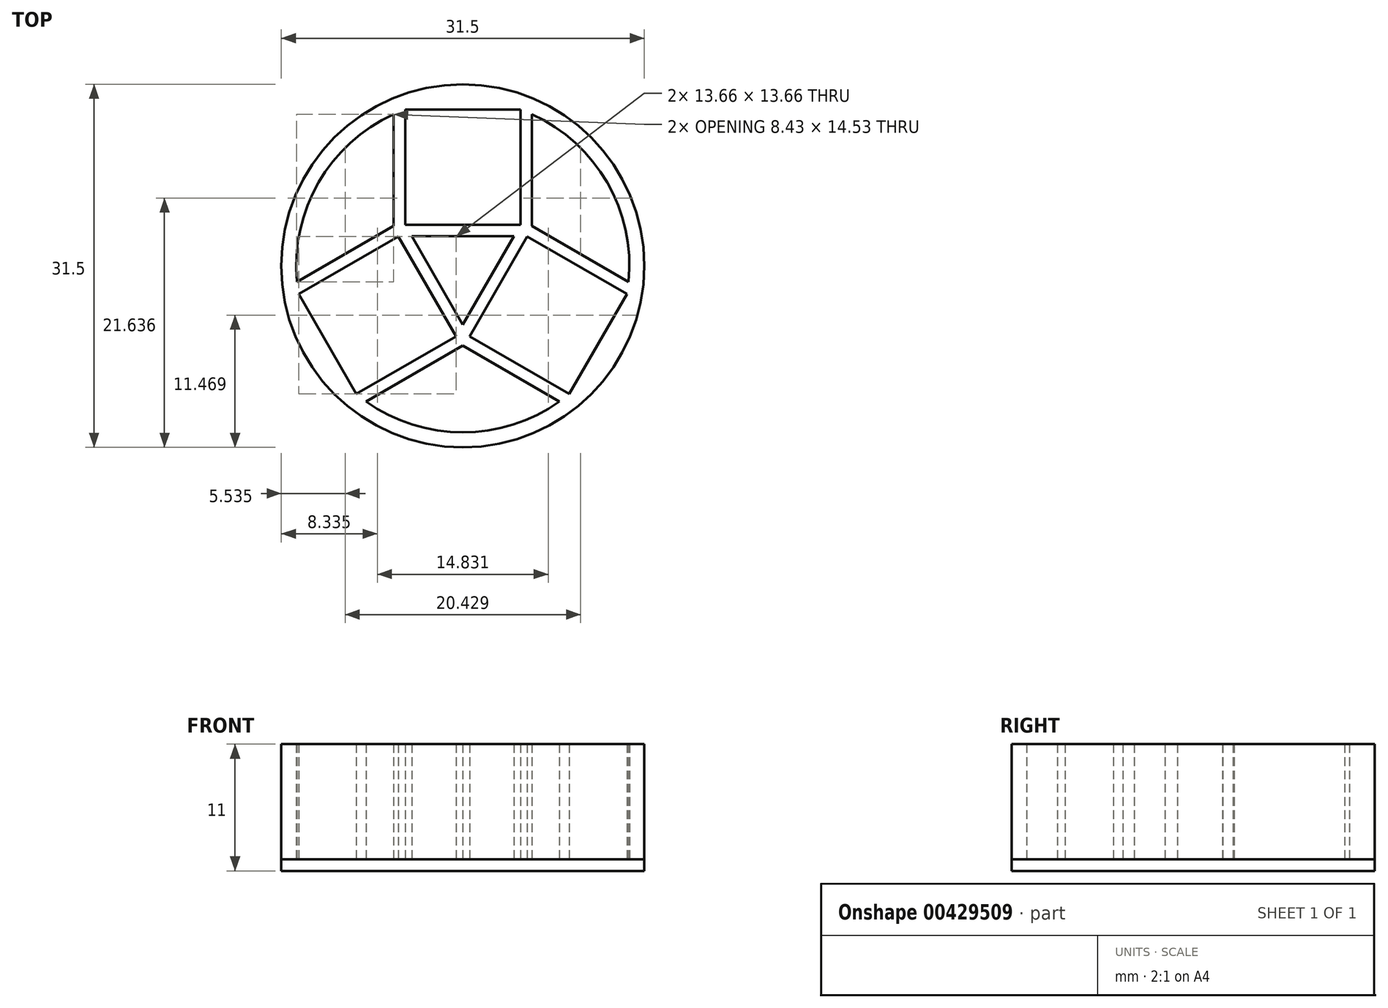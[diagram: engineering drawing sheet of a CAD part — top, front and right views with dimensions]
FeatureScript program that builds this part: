
annotation { "Feature Type Name" : "Feature", "Feature Type Description" : "" }
export const myFeature = defineFeature(function(context is Context, id is Id, definition is map)
    precondition{}
    {
        {
            var Q0;
            Q0=qCreatedBy(makeId("Top.planeOp"),FACE);
            var sketch = newSketch(context, id + "F0", { "sketchPlane" : qUnion([Q0])});
            skLineSegment(sketch, "E0.bottom", {"start": v(-5, 13.56) * mm, "end": v(5, 13.56) * mm});
            skLineSegment(sketch, "E0.top", {"start": v(-5, 3.56) * mm, "end": v(5, 3.56) * mm});
            skLineSegment(sketch, "E0.left", {"start": v(-5, 13.56) * mm, "end": v(-5, 3.56) * mm});
            skLineSegment(sketch, "E0.right", {"start": v(5, 13.56) * mm, "end": v(5, 3.56) * mm});
            skCircle(sketch, "E1", {"center": v(0, 0) * mm, "radius": 15.75 * mm});
            skLineSegment(sketch, "E2.0", {"start": v(-6, 14.56) * mm, "end": v(6, 14.56) * mm});
            skLineSegment(sketch, "E2.1", {"start": v(-6, 14.56) * mm, "end": v(-6, 2.56) * mm});
            skLineSegment(sketch, "E2.2", {"start": v(-6, 2.56) * mm, "end": v(6, 2.56) * mm});
            skLineSegment(sketch, "E2.3", {"start": v(6, 14.56) * mm, "end": v(6, 2.56) * mm});
            skLineSegment(sketch, "E3.1.0", {"start": v(-9.61, -12.48) * mm, "end": v(0.78, -6.48) * mm});
            skLineSegment(sketch, "E3.1.1", {"start": v(-9.25, -11.11) * mm, "end": v(-0.59, -6.11) * mm});
            skLineSegment(sketch, "E3.1.2", {"start": v(-9.61, -12.48) * mm, "end": v(-15.61, -2.09) * mm});
            skLineSegment(sketch, "E3.1.3", {"start": v(-9.25, -11.11) * mm, "end": v(-14.25, -2.45) * mm});
            skLineSegment(sketch, "E3.1.4", {"start": v(-14.25, -2.45) * mm, "end": v(-5.59, 2.55) * mm});
            skLineSegment(sketch, "E3.1.5", {"start": v(-15.61, -2.09) * mm, "end": v(-5.22, 3.91) * mm});
            skLineSegment(sketch, "E3.1.6", {"start": v(0.78, -6.48) * mm, "end": v(-5.22, 3.91) * mm});
            skLineSegment(sketch, "E3.1.7", {"start": v(-0.59, -6.11) * mm, "end": v(-5.59, 2.55) * mm});
            skLineSegment(sketch, "E3.2.0", {"start": v(15.61, -2.09) * mm, "end": v(5.22, 3.91) * mm});
            skLineSegment(sketch, "E3.2.1", {"start": v(14.25, -2.45) * mm, "end": v(5.59, 2.55) * mm});
            skLineSegment(sketch, "E3.2.2", {"start": v(15.61, -2.09) * mm, "end": v(9.61, -12.48) * mm});
            skLineSegment(sketch, "E3.2.3", {"start": v(14.25, -2.45) * mm, "end": v(9.25, -11.11) * mm});
            skLineSegment(sketch, "E3.2.4", {"start": v(9.25, -11.11) * mm, "end": v(0.59, -6.11) * mm});
            skLineSegment(sketch, "E3.2.5", {"start": v(9.61, -12.48) * mm, "end": v(-0.78, -6.48) * mm});
            skLineSegment(sketch, "E3.2.6", {"start": v(5.22, 3.91) * mm, "end": v(-0.78, -6.48) * mm});
            skLineSegment(sketch, "E3.2.7", {"start": v(5.59, 2.55) * mm, "end": v(0.59, -6.11) * mm});
            skCircle(sketch, "E4", {"center": v(0, 0) * mm, "radius": 14.45 * mm});
            skSolve(sketch);
        }
        {
            var Q0;
            {var subQ5=sQuery(id+"F0.wireOp",EDGE,"E3.1.2");Q0=makeQuery(id+"F0.imprint","IMPRINT",FACE,{"disambiguationData":[TD([[makeQuery(id+"F0.imprint","IMPRINT",EDGE,{"derivedFrom":subQ5}),-1.0]])]});}
            var Q1;
            {var subQ5=sQuery(id+"F0.wireOp",EDGE,"E3.2.2");Q1=makeQuery(id+"F0.imprint","IMPRINT",FACE,{"disambiguationData":[TD([[makeQuery(id+"F0.imprint","IMPRINT",EDGE,{"derivedFrom":subQ5}),-1.0]])]});}
            var Q2;
            Q2=makeQuery(id+"F0.imprint","IMPRINT",FACE,{"disambiguationData":[TD([[makeQuery(id+"F0.imprint","IMPRINT",EDGE,{"derivedFrom":sQuery(id+"F0.wireOp",EDGE,"E0.top")}),-1.0]])]});
            var Q3;
            {var subQ0=sQuery(id+"F0.wireOp",EDGE,"E4");var subQ1=sQuery(id+"F0.wireOp",EDGE,"E2.1");var subQ2=makeQuery(id+"F0.imprint","INTERSECT",VERTEX,{"derivedFrom":[subQ1,subQ0]});Q3=makeQuery(id+"F0.imprint","IMPRINT",FACE,{"disambiguationData":[TD([[makeQuery(id+"F0.imprint","IMPRINT",EDGE,{"disambiguationData":[TD([[subQ2,-1.0]])],"derivedFrom":subQ1}),-1.0]])]});}
            var Q4;
            {var subQ0=sQuery(id+"F0.wireOp",EDGE,"E3.1.0");var subQ5=sQuery(id+"F0.wireOp",EDGE,"E4");var subQ6=makeQuery(id+"F0.imprint","INTERSECT",VERTEX,{"derivedFrom":[subQ0,subQ5]});Q4=makeQuery(id+"F0.imprint","IMPRINT",FACE,{"disambiguationData":[TD([[makeQuery(id+"F0.imprint","IMPRINT",EDGE,{"disambiguationData":[TD([[subQ6,-1.0]])],"derivedFrom":subQ5}),-1.0]])]});}
            var Q5;
            {var subQ0=sQuery(id+"F0.wireOp",EDGE,"E2.3");var subQ5=sQuery(id+"F0.wireOp",EDGE,"E4");var subQ7=makeQuery(id+"F0.imprint","INTERSECT",VERTEX,{"derivedFrom":[subQ0,subQ5]});Q5=makeQuery(id+"F0.imprint","IMPRINT",FACE,{"disambiguationData":[TD([[makeQuery(id+"F0.imprint","IMPRINT",EDGE,{"disambiguationData":[TD([[subQ7,1.0]])],"derivedFrom":subQ5}),-1.0]])]});}
            var Q6;
            {var subQ0=sQuery(id+"F0.wireOp",EDGE,"E3.1.6");var subQ1=sQuery(id+"F0.wireOp",EDGE,"E2.2");var subQ2=makeQuery(id+"F0.imprint","INTERSECT",VERTEX,{"derivedFrom":[subQ1,subQ0]});Q6=makeQuery(id+"F0.imprint","IMPRINT",FACE,{"disambiguationData":[TD([[makeQuery(id+"F0.imprint","IMPRINT",EDGE,{"disambiguationData":[TD([[subQ2,-1.0]])],"derivedFrom":subQ1}),-1.0]])]});}
            var Q7;
            {var subQ0=sQuery(id+"F0.wireOp",EDGE,"E2.0");Q7=makeQuery(id+"F0.imprint","IMPRINT",FACE,{"disambiguationData":[TD([[makeQuery(id+"F0.imprint","IMPRINT",EDGE,{"derivedFrom":subQ0}),1.0]])]});}
            var Q8;
            {var subQ0=sQuery(id+"F0.wireOp",EDGE,"E3.1.2");Q8=makeQuery(id+"F0.imprint","IMPRINT",FACE,{"disambiguationData":[TD([[makeQuery(id+"F0.imprint","IMPRINT",EDGE,{"derivedFrom":subQ0}),1.0]])]});}
            var Q9;
            {var subQ0=sQuery(id+"F0.wireOp",EDGE,"E3.2.2");Q9=makeQuery(id+"F0.imprint","IMPRINT",FACE,{"disambiguationData":[TD([[makeQuery(id+"F0.imprint","IMPRINT",EDGE,{"derivedFrom":subQ0}),1.0]])]});}
            var Q10;
            Q10=makeQuery(id+"F0.imprint","IMPRINT",FACE,{"disambiguationData":[TD([[makeQuery(id+"F0.imprint","IMPRINT",EDGE,{"derivedFrom":sQuery(id+"F0.wireOp",EDGE,"E0.bottom")}),-1.0]])]});
            var Q11;
            {var subQ0=sQuery(id+"F0.wireOp",EDGE,"E0.bottom");Q11=makeQuery(id+"F0.imprint","IMPRINT",FACE,{"disambiguationData":[TD([[makeQuery(id+"F0.imprint","IMPRINT",EDGE,{"derivedFrom":subQ0}),1.0]])]});}
            var Q12;
            Q12=makeQuery(id+"F0.imprint","IMPRINT",FACE,{"disambiguationData":[TD([[makeQuery(id+"F0.imprint","IMPRINT",EDGE,{"derivedFrom":sQuery(id+"F0.wireOp",EDGE,"E3.1.1")}),1.0]])]});
            var Q13;
            {var subQ0=sQuery(id+"F0.wireOp",EDGE,"E3.1.3");Q13=makeQuery(id+"F0.imprint","IMPRINT",FACE,{"disambiguationData":[TD([[makeQuery(id+"F0.imprint","IMPRINT",EDGE,{"derivedFrom":subQ0}),1.0]])]});}
            var Q14;
            Q14=makeQuery(id+"F0.imprint","IMPRINT",FACE,{"disambiguationData":[TD([[makeQuery(id+"F0.imprint","IMPRINT",EDGE,{"derivedFrom":sQuery(id+"F0.wireOp",EDGE,"E3.2.1")}),1.0]])]});
            var Q15;
            {var subQ0=sQuery(id+"F0.wireOp",EDGE,"E3.2.3");Q15=makeQuery(id+"F0.imprint","IMPRINT",FACE,{"disambiguationData":[TD([[makeQuery(id+"F0.imprint","IMPRINT",EDGE,{"derivedFrom":subQ0}),1.0]])]});}
            var Q16;
            {var subQ0=sQuery(id+"F0.wireOp",EDGE,"E2.1");var subQ5=sQuery(id+"F0.wireOp",EDGE,"E4");var subQ6=makeQuery(id+"F0.imprint","INTERSECT",VERTEX,{"derivedFrom":[subQ0,subQ5]});Q16=makeQuery(id+"F0.imprint","IMPRINT",FACE,{"disambiguationData":[TD([[makeQuery(id+"F0.imprint","IMPRINT",EDGE,{"disambiguationData":[TD([[subQ6,-1.0]])],"derivedFrom":subQ5}),-1.0]])]});}
            var Q17;
            {var subQ7=sQuery(id+"F0.wireOp",EDGE,"E3.1.1");Q17=makeQuery(id+"F0.imprint","IMPRINT",FACE,{"disambiguationData":[TD([[makeQuery(id+"F0.imprint","IMPRINT",EDGE,{"derivedFrom":subQ7}),-1.0]])]});}
            var Q18;
            {var subQ0=sQuery(id+"F0.wireOp",EDGE,"E4");var subQ1=sQuery(id+"F0.wireOp",EDGE,"E2.3");var subQ2=makeQuery(id+"F0.imprint","INTERSECT",VERTEX,{"derivedFrom":[subQ1,subQ0]});Q18=makeQuery(id+"F0.imprint","IMPRINT",FACE,{"disambiguationData":[TD([[makeQuery(id+"F0.imprint","IMPRINT",EDGE,{"disambiguationData":[TD([[subQ2,-1.0]])],"derivedFrom":subQ1}),1.0]])]});}
            var Q19;
            {var subQ16=sQuery(id+"F0.wireOp",EDGE,"E3.2.1");Q19=makeQuery(id+"F0.imprint","IMPRINT",FACE,{"disambiguationData":[TD([[makeQuery(id+"F0.imprint","IMPRINT",EDGE,{"derivedFrom":subQ16}),-1.0]])]});}
            var Q20;
            {var subQ0=sQuery(id+"F0.wireOp",EDGE,"E4");var subQ1=sQuery(id+"F0.wireOp",EDGE,"E3.1.0");var subQ2=makeQuery(id+"F0.imprint","INTERSECT",VERTEX,{"derivedFrom":[subQ1,subQ0]});Q20=makeQuery(id+"F0.imprint","IMPRINT",FACE,{"disambiguationData":[TD([[makeQuery(id+"F0.imprint","IMPRINT",EDGE,{"disambiguationData":[TD([[subQ2,-1.0]])],"derivedFrom":subQ1}),-1.0]])]});}
            var Q21;
            {var subQ5=sQuery(id+"F0.wireOp",EDGE,"E2.0");Q21=makeQuery(id+"F0.imprint","IMPRINT",FACE,{"disambiguationData":[TD([[makeQuery(id+"F0.imprint","IMPRINT",EDGE,{"derivedFrom":subQ5}),-1.0]])]});}
            var Q22;
            {var subQ0=sQuery(id+"F0.wireOp",EDGE,"E2.3");var subQ1=sQuery(id+"F0.wireOp",EDGE,"E2.2");var subQ2=makeQuery(id+"F0.imprint","INTERSECT",VERTEX,{"derivedFrom":[subQ1,subQ0]});Q22=makeQuery(id+"F0.imprint","IMPRINT",FACE,{"disambiguationData":[TD([[makeQuery(id+"F0.imprint","IMPRINT",EDGE,{"disambiguationData":[TD([[subQ2,1.0]])],"derivedFrom":subQ1}),1.0]])]});}
            var Q23;
            {var subQ0=sQuery(id+"F0.wireOp",EDGE,"E3.1.6");var subQ1=sQuery(id+"F0.wireOp",EDGE,"E3.1.0");var subQ2=makeQuery(id+"F0.imprint","INTERSECT",VERTEX,{"derivedFrom":[subQ1,subQ0]});Q23=makeQuery(id+"F0.imprint","IMPRINT",FACE,{"disambiguationData":[TD([[makeQuery(id+"F0.imprint","IMPRINT",EDGE,{"disambiguationData":[TD([[subQ2,1.0]])],"derivedFrom":subQ1}),1.0]])]});}
            var Q24;
            {var subQ0=sQuery(id+"F0.wireOp",EDGE,"E2.2");var subQ1=sQuery(id+"F0.wireOp",EDGE,"E2.1");var subQ2=makeQuery(id+"F0.imprint","INTERSECT",VERTEX,{"derivedFrom":[subQ1,subQ0]});Q24=makeQuery(id+"F0.imprint","IMPRINT",FACE,{"disambiguationData":[TD([[makeQuery(id+"F0.imprint","IMPRINT",EDGE,{"disambiguationData":[TD([[subQ2,1.0]])],"derivedFrom":subQ1}),1.0]])]});}
            extrude(context, id + "F1", {"entities" : qUnion([Q0, Q1, Q2, Q3, Q4, Q5, Q6, Q7, Q8, Q9, Q10, Q11, Q12, Q13, Q14, Q15, Q16, Q17, Q18, Q19, Q20, Q21, Q22, Q23, Q24]), "depth" : -1 * mm});
        }
        {
            var Q0;
            {var subQ7=sQuery(id+"F0.wireOp",EDGE,"E3.1.1");Q0=makeQuery(id+"F0.imprint","IMPRINT",FACE,{"disambiguationData":[TD([[makeQuery(id+"F0.imprint","IMPRINT",EDGE,{"derivedFrom":subQ7}),-1.0]])]});}
            var Q1;
            {var subQ0=sQuery(id+"F0.wireOp",EDGE,"E2.1");var subQ5=sQuery(id+"F0.wireOp",EDGE,"E4");var subQ6=makeQuery(id+"F0.imprint","INTERSECT",VERTEX,{"derivedFrom":[subQ0,subQ5]});Q1=makeQuery(id+"F0.imprint","IMPRINT",FACE,{"disambiguationData":[TD([[makeQuery(id+"F0.imprint","IMPRINT",EDGE,{"disambiguationData":[TD([[subQ6,-1.0]])],"derivedFrom":subQ5}),-1.0]])]});}
            var Q2;
            {var subQ0=sQuery(id+"F0.wireOp",EDGE,"E0.bottom");Q2=makeQuery(id+"F0.imprint","IMPRINT",FACE,{"disambiguationData":[TD([[makeQuery(id+"F0.imprint","IMPRINT",EDGE,{"derivedFrom":subQ0}),1.0]])]});}
            var Q3;
            {var subQ0=sQuery(id+"F0.wireOp",EDGE,"E3.1.2");Q3=makeQuery(id+"F0.imprint","IMPRINT",FACE,{"disambiguationData":[TD([[makeQuery(id+"F0.imprint","IMPRINT",EDGE,{"derivedFrom":subQ0}),1.0]])]});}
            var Q4;
            {var subQ0=sQuery(id+"F0.wireOp",EDGE,"E2.0");Q4=makeQuery(id+"F0.imprint","IMPRINT",FACE,{"disambiguationData":[TD([[makeQuery(id+"F0.imprint","IMPRINT",EDGE,{"derivedFrom":subQ0}),1.0]])]});}
            var Q5;
            {var subQ0=sQuery(id+"F0.wireOp",EDGE,"E2.3");var subQ5=sQuery(id+"F0.wireOp",EDGE,"E4");var subQ7=makeQuery(id+"F0.imprint","INTERSECT",VERTEX,{"derivedFrom":[subQ0,subQ5]});Q5=makeQuery(id+"F0.imprint","IMPRINT",FACE,{"disambiguationData":[TD([[makeQuery(id+"F0.imprint","IMPRINT",EDGE,{"disambiguationData":[TD([[subQ7,1.0]])],"derivedFrom":subQ5}),-1.0]])]});}
            var Q6;
            {var subQ0=sQuery(id+"F0.wireOp",EDGE,"E3.1.0");var subQ5=sQuery(id+"F0.wireOp",EDGE,"E4");var subQ6=makeQuery(id+"F0.imprint","INTERSECT",VERTEX,{"derivedFrom":[subQ0,subQ5]});Q6=makeQuery(id+"F0.imprint","IMPRINT",FACE,{"disambiguationData":[TD([[makeQuery(id+"F0.imprint","IMPRINT",EDGE,{"disambiguationData":[TD([[subQ6,-1.0]])],"derivedFrom":subQ5}),-1.0]])]});}
            var Q7;
            Q7=makeQuery(id+"F0.imprint","IMPRINT",FACE,{"disambiguationData":[TD([[makeQuery(id+"F0.imprint","IMPRINT",EDGE,{"derivedFrom":sQuery(id+"F0.wireOp",EDGE,"E0.top")}),-1.0]])]});
            var Q8;
            {var subQ16=sQuery(id+"F0.wireOp",EDGE,"E3.2.1");Q8=makeQuery(id+"F0.imprint","IMPRINT",FACE,{"disambiguationData":[TD([[makeQuery(id+"F0.imprint","IMPRINT",EDGE,{"derivedFrom":subQ16}),-1.0]])]});}
            var Q9;
            {var subQ0=sQuery(id+"F0.wireOp",EDGE,"E3.1.3");Q9=makeQuery(id+"F0.imprint","IMPRINT",FACE,{"disambiguationData":[TD([[makeQuery(id+"F0.imprint","IMPRINT",EDGE,{"derivedFrom":subQ0}),1.0]])]});}
            var Q10;
            {var subQ0=sQuery(id+"F0.wireOp",EDGE,"E3.2.2");Q10=makeQuery(id+"F0.imprint","IMPRINT",FACE,{"disambiguationData":[TD([[makeQuery(id+"F0.imprint","IMPRINT",EDGE,{"derivedFrom":subQ0}),1.0]])]});}
            var Q11;
            {var subQ5=sQuery(id+"F0.wireOp",EDGE,"E3.2.2");Q11=makeQuery(id+"F0.imprint","IMPRINT",FACE,{"disambiguationData":[TD([[makeQuery(id+"F0.imprint","IMPRINT",EDGE,{"derivedFrom":subQ5}),-1.0]])]});}
            var Q12;
            {var subQ0=sQuery(id+"F0.wireOp",EDGE,"E3.2.3");Q12=makeQuery(id+"F0.imprint","IMPRINT",FACE,{"disambiguationData":[TD([[makeQuery(id+"F0.imprint","IMPRINT",EDGE,{"derivedFrom":subQ0}),1.0]])]});}
            var Q13;
            {var subQ5=sQuery(id+"F0.wireOp",EDGE,"E3.1.2");Q13=makeQuery(id+"F0.imprint","IMPRINT",FACE,{"disambiguationData":[TD([[makeQuery(id+"F0.imprint","IMPRINT",EDGE,{"derivedFrom":subQ5}),-1.0]])]});}
            var Q14;
            {var subQ5=sQuery(id+"F0.wireOp",EDGE,"E2.0");Q14=makeQuery(id+"F0.imprint","IMPRINT",FACE,{"disambiguationData":[TD([[makeQuery(id+"F0.imprint","IMPRINT",EDGE,{"derivedFrom":subQ5}),-1.0]])]});}
            var Q15;
            {var subQ0=sQuery(id+"F0.wireOp",EDGE,"E2.3");var subQ1=sQuery(id+"F0.wireOp",EDGE,"E2.2");var subQ2=makeQuery(id+"F0.imprint","INTERSECT",VERTEX,{"derivedFrom":[subQ1,subQ0]});Q15=makeQuery(id+"F0.imprint","IMPRINT",FACE,{"disambiguationData":[TD([[makeQuery(id+"F0.imprint","IMPRINT",EDGE,{"disambiguationData":[TD([[subQ2,1.0]])],"derivedFrom":subQ1}),1.0]])]});}
            var Q16;
            {var subQ0=sQuery(id+"F0.wireOp",EDGE,"E3.1.6");var subQ1=sQuery(id+"F0.wireOp",EDGE,"E3.1.0");var subQ2=makeQuery(id+"F0.imprint","INTERSECT",VERTEX,{"derivedFrom":[subQ1,subQ0]});Q16=makeQuery(id+"F0.imprint","IMPRINT",FACE,{"disambiguationData":[TD([[makeQuery(id+"F0.imprint","IMPRINT",EDGE,{"disambiguationData":[TD([[subQ2,1.0]])],"derivedFrom":subQ1}),1.0]])]});}
            var Q17;
            {var subQ0=sQuery(id+"F0.wireOp",EDGE,"E2.2");var subQ1=sQuery(id+"F0.wireOp",EDGE,"E2.1");var subQ2=makeQuery(id+"F0.imprint","INTERSECT",VERTEX,{"derivedFrom":[subQ1,subQ0]});Q17=makeQuery(id+"F0.imprint","IMPRINT",FACE,{"disambiguationData":[TD([[makeQuery(id+"F0.imprint","IMPRINT",EDGE,{"disambiguationData":[TD([[subQ2,1.0]])],"derivedFrom":subQ1}),1.0]])]});}
            extrude(context, id + "F2", {"entities" : qUnion([Q0, Q1, Q2, Q3, Q4, Q5, Q6, Q7, Q8, Q9, Q10, Q11, Q12, Q13, Q14, Q15, Q16, Q17]), "depth" : 10 * mm});
        }
    });
